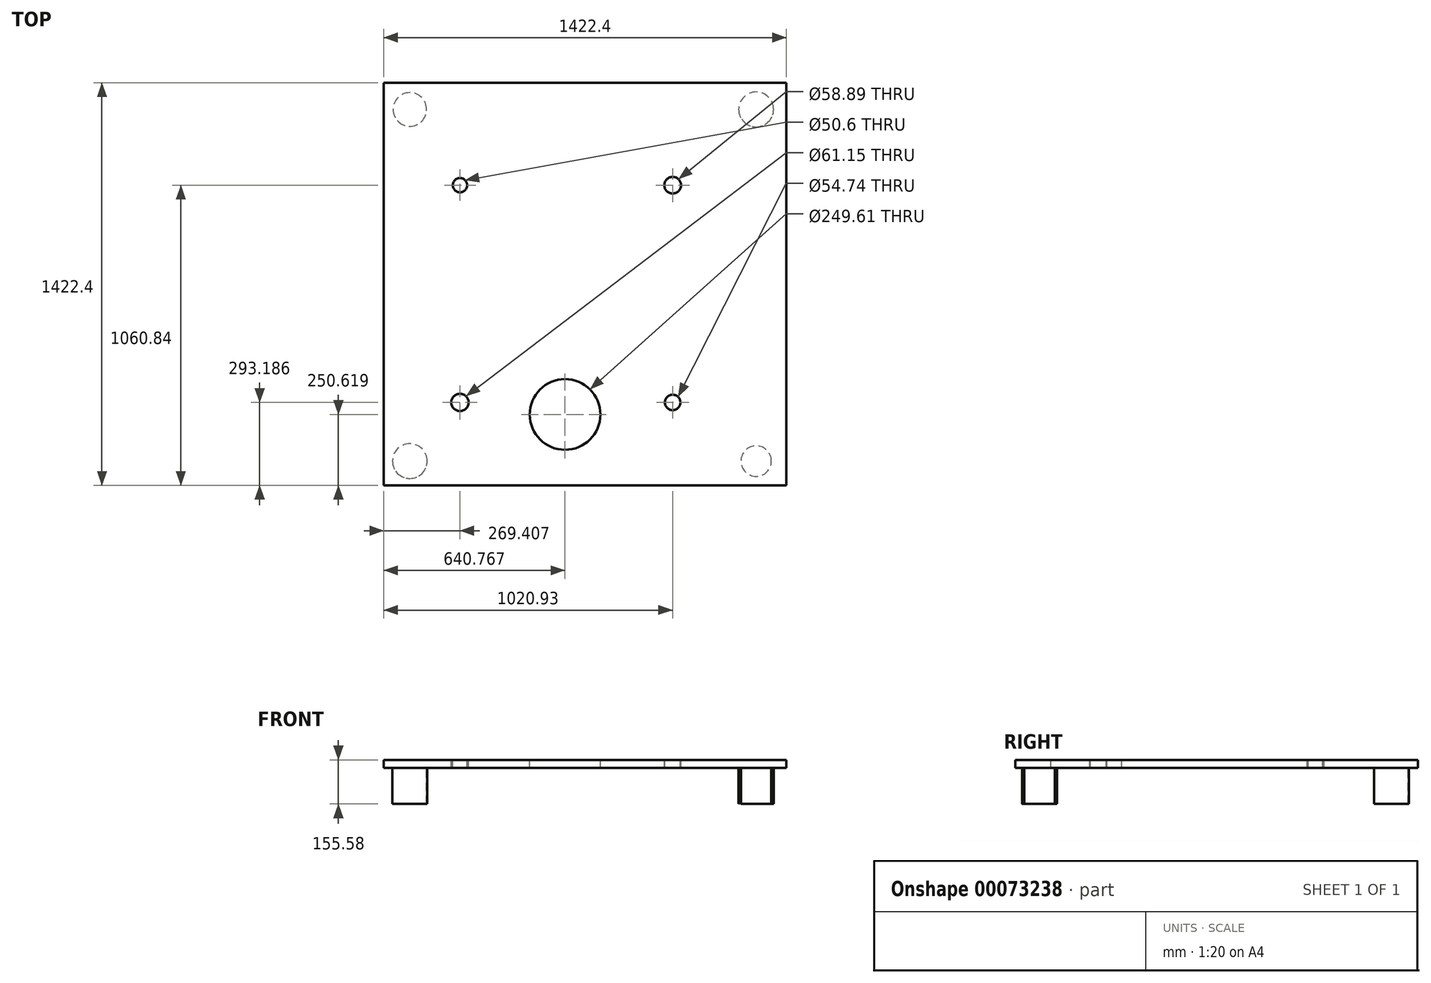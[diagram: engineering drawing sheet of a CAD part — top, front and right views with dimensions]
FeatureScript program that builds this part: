
annotation { "Feature Type Name" : "Feature", "Feature Type Description" : "" }
export const myFeature = defineFeature(function(context is Context, id is Id, definition is map)
    precondition{}
    {
        {
            var Q0;
            Q0=qCreatedBy(makeId("Top.planeOp"),FACE);
            var sketch = newSketch(context, id + "F0", { "sketchPlane" : qUnion([Q0])});
            skLineSegment(sketch, "E0.bottom", {"start": v(-724.61, 1070.16) * mm, "end": v(697.79, 1070.16) * mm});
            skLineSegment(sketch, "E0.top", {"start": v(-724.61, -352.24) * mm, "end": v(697.79, -352.24) * mm});
            skLineSegment(sketch, "E0.left", {"start": v(-724.61, 1070.16) * mm, "end": v(-724.61, -352.24) * mm});
            skLineSegment(sketch, "E0.right", {"start": v(697.79, 1070.16) * mm, "end": v(697.79, -352.24) * mm});
            skSolve(sketch);
        }
        {
            var Q0;
            Q0=makeQuery(id+"F0.imprint","IMPRINT",FACE,{"disambiguationData":[TD([[makeQuery(id+"F0.imprint","IMPRINT",EDGE,{"derivedFrom":sQuery(id+"F0.wireOp",EDGE,"E0.bottom")}),-1.0]])]});
            extrude(context, id + "F1", {"entities" : qUnion([Q0]), "depth" : 28.57 * mm});
        }
        {
            var Q0;
            Q0=makeQuery(id+"F1.opExtrude","CAP_FACE",FACE,{"disambiguationData":[OSD([sQuery(id+"F0.wireOp",EDGE,"E0.bottom"),sQuery(id+"F0.wireOp",EDGE,"E0.top"),sQuery(id+"F0.wireOp",EDGE,"E0.left"),sQuery(id+"F0.wireOp",EDGE,"E0.right")])],"isStart":true});
            var sketch = newSketch(context, id + "F2", { "sketchPlane" : qUnion([Q0])});
            skCircle(sketch, "E1", {"center": v(591.24, 266.28) * mm, "radius": 53.88 * mm});
            skCircle(sketch, "E2", {"center": v(591.24, -976.19) * mm, "radius": 61.7 * mm});
            skCircle(sketch, "E3", {"center": v(-632.2, -976.19) * mm, "radius": 59.41 * mm});
            skCircle(sketch, "E4", {"center": v(-632.2, 266.28) * mm, "radius": 61.39 * mm});
            skSolve(sketch);
        }
        {
            var Q0;
            Q0 = qSketchRegion(id + "F2", true);
            extrude(context, id + "F3", {"entities" : qUnion([Q0]), "operationType" : NewBodyOperationType.ADD, "depth" : 127 * mm});
        }
        {
            var Q0;
            Q0=makeQuery(id+"F1.opExtrude","CAP_FACE",FACE,{"disambiguationData":[OSD([sQuery(id+"F0.wireOp",EDGE,"E0.bottom"),sQuery(id+"F0.wireOp",EDGE,"E0.top"),sQuery(id+"F0.wireOp",EDGE,"E0.left"),sQuery(id+"F0.wireOp",EDGE,"E0.right")])],"isStart":false});
            var sketch = newSketch(context, id + "F4", { "sketchPlane" : qUnion([Q0])});
            skCircle(sketch, "E5", {"center": v(296.32, 708.6) * mm, "radius": 29.45 * mm});
            skCircle(sketch, "E6", {"center": v(-455.2, 708.6) * mm, "radius": 25.3 * mm});
            skCircle(sketch, "E7", {"center": v(-455.2, -59.05) * mm, "radius": 30.57 * mm});
            skCircle(sketch, "E8", {"center": v(296.32, -59.05) * mm, "radius": 27.37 * mm});
            skSolve(sketch);
        }
        {
            var Q0;
            Q0 = qSketchRegion(id + "F4", true);
            extrude(context, id + "F5", {"entities" : qUnion([Q0]), "operationType" : NewBodyOperationType.REMOVE, "oppositeDirection" : true, "depth" : 428.46 * mm});
        }
        {
            var Q0;
            Q0=makeQuery(id+"F4.imprint","IMPRINT",FACE,{"disambiguationData":[TD([[makeQuery(id+"F4.imprint","IMPRINT",EDGE,{"derivedFrom":sQuery(id+"F4.wireOp",EDGE,"E5")}),-1.0]])]});
            var sketch = newSketch(context, id + "F6", { "sketchPlane" : qUnion([Q0])});
            skCircle(sketch, "E9", {"center": v(-83.84, -101.62) * mm, "radius": 124.8 * mm});
            skPoint(sketch, "E9.first.point", {"position": v(-108.52, -223.96) * mm});
            skPoint(sketch, "E9.second.point", {"position": v(35.78, -66.02) * mm});
            skPoint(sketch, "E9.third.point", {"position": v(-200.72, -57.84) * mm});
            skSolve(sketch);
        }
        {
            var Q0;
            Q0 = qSketchRegion(id + "F6", true);
            var Q1;
            Q1=sQuery(id+"F6.wireOp",EDGE,"E9");
            extrude(context, id + "F7", {"entities" : qUnion([Q0]), "operationType" : NewBodyOperationType.REMOVE, "surfaceEntities" : qUnion([Q1]), "oppositeDirection" : true, "depth" : 511.5 * mm});
        }
    });
